# Revit family: Faucet_Touchless-Lavatory-KOHLER-ELOSIS-K-18055T_1
name_source: partatom
category: Plumbing Fixtures
revit_build: Autodesk Revit 2017 (Build: 20160225_1515(x64)
units: mm (PartAtom-declared; Revit-internal decimal feet)

## family parameters
Cut with Voids When Loaded = No
Host = Face
OmniClass Number = 23.31.11.00
OmniClass Title = Faucets
Part Type = Normal
Room Calculation Point = No
Round Connector Dimension = Use Diameter
Shared = No

## types (2) — shared parameters
ADA Compliant = No
Assembly Code = D2010
CW Connection = Yes
Cold Water Inlet = Cold Water Inlet
Date Modified = 11/27/2020
Default Elevation = 36"
Drain Included = Yes
Finish = Kohler-Metal-CP-Polished_Chrome
HW Connection = Yes
Height = 5 1/2"
Length = 4 13/16"
Manufacturer = KOHLER Co.
Master Format 2014 = 22 41 39
Master Format 2014 Name = Residential Faucets, Supplies, and Trim
Material = Brass Construction
Product Name = ELOSIS
Spout Reach = 4 13/16"
Tempered Water Inlet Dia = 1/2"
URL = http://www.kohler.com.cn
Vent Connection = No
Waste Connection = No
Waste Water Outlet = Waste Water Outlet
WaterSense Certified = No
Width = 2 7/16"

## per-type parameters (varying)
| type | Cold Water Inlet Dia | Description | Dist 1 | Flow Rate | Hot Water Inlet | Model | Pressure | Product Page URL | Type | With Handle | Without Handle |
| With Handle, CP-Polished Chrome | 1/2" | Sensor Faucet-Mixer-DC | 1/2" | 2 GPM | Hot Water Inlet | K-18055T-CP | 60.00 psi |  | 1 | Yes | No |
| Without Handle, CP-Polished Chrome | 0" | Daishi basin induction faucet-DC | 0" | 1 GPM | Tempered Water Inlet | K-18055T-B-CP | 43.51 psi | https://www.kohler.com.cn | 2 | No | Yes |

## geometry (parser evidence)
native form markers: Sweep x5
no freeform markers — native parametric forms only
